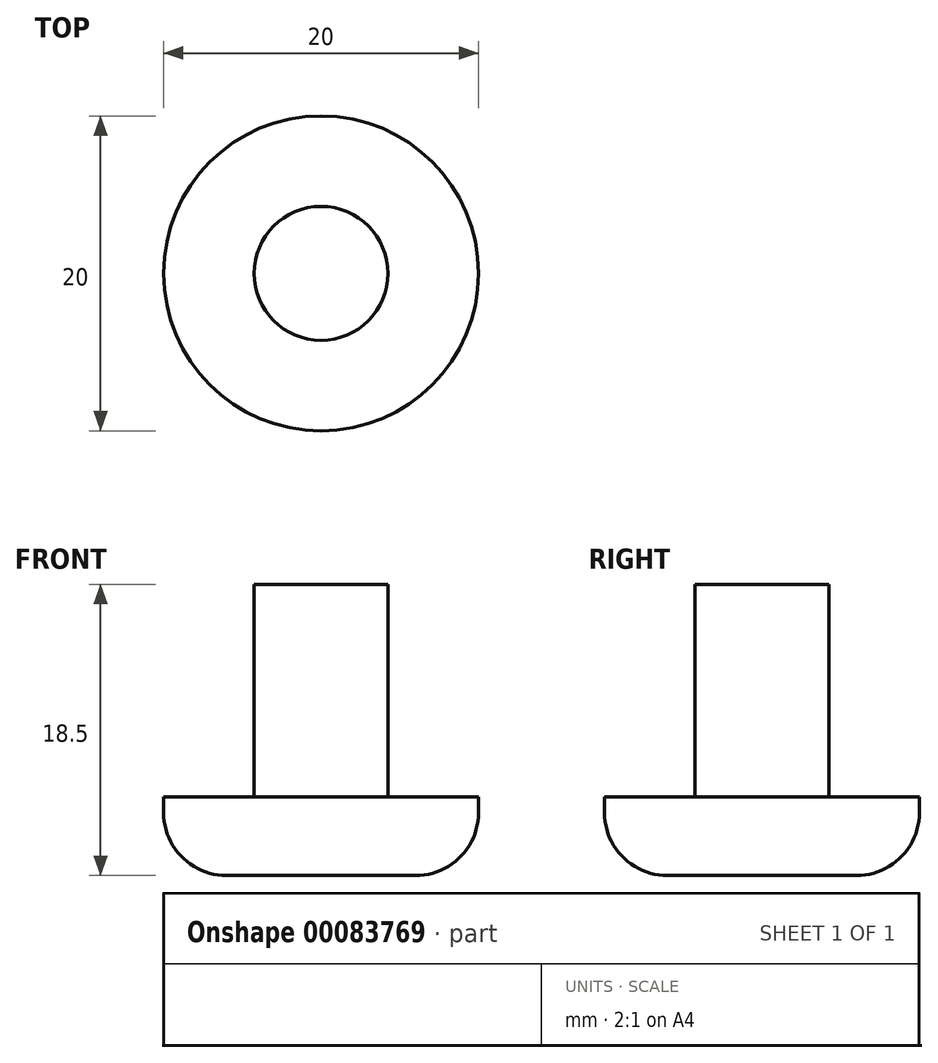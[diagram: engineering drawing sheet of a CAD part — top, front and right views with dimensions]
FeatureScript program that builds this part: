
annotation { "Feature Type Name" : "Feature", "Feature Type Description" : "" }
export const myFeature = defineFeature(function(context is Context, id is Id, definition is map)
    precondition{}
    {
        {
            var Q0;
            Q0=qCreatedBy(makeId("Top.planeOp"),FACE);
            var sketch = newSketch(context, id + "F0", { "sketchPlane" : qUnion([Q0])});
            skCircle(sketch, "E0", {"center": v(0, 0) * mm, "radius": 4.25 * mm});
            skSolve(sketch);
        }
        {
            var Q0;
            Q0=makeQuery(id+"F0.imprint","IMPRINT",FACE,{"disambiguationData":[TD([[makeQuery(id+"F0.imprint","IMPRINT",EDGE,{"derivedFrom":sQuery(id+"F0.wireOp",EDGE,"E0")}),1.0]])]});
            extrude(context, id + "F1", {"entities" : qUnion([Q0]), "depth" : 13.5 * mm});
        }
        {
            var Q0;
            Q0=makeQuery(id+"F1.opExtrude","CAP_FACE",FACE,{"disambiguationData":[OSD([sQuery(id+"F0.wireOp",EDGE,"E0")])],"isStart":true});
            var sketch = newSketch(context, id + "F2", { "sketchPlane" : qUnion([Q0])});
            skCircle(sketch, "E1", {"center": v(0, 0) * mm, "radius": 10 * mm});
            skSolve(sketch);
        }
        {
            var Q0;
            Q0 = qSketchRegion(id + "F2", true);
            extrude(context, id + "F3", {"entities" : qUnion([Q0]), "operationType" : NewBodyOperationType.ADD, "depth" : 5 * mm});
        }
        {
            var Q0;
            Q0=makeQuery(id+"F3.opExtrude","CAP_EDGE",EDGE,{"disambiguationData":[OSD([sQuery(id+"F2.wireOp",EDGE,"E1")])],"isStart":false});
            fillet(context, id + "F4", {"entities" : qUnion([Q0]), "radius" : 4 * mm, "tangentPropagation" : true, "allowEdgeOverflow" : false});
        }
    });
